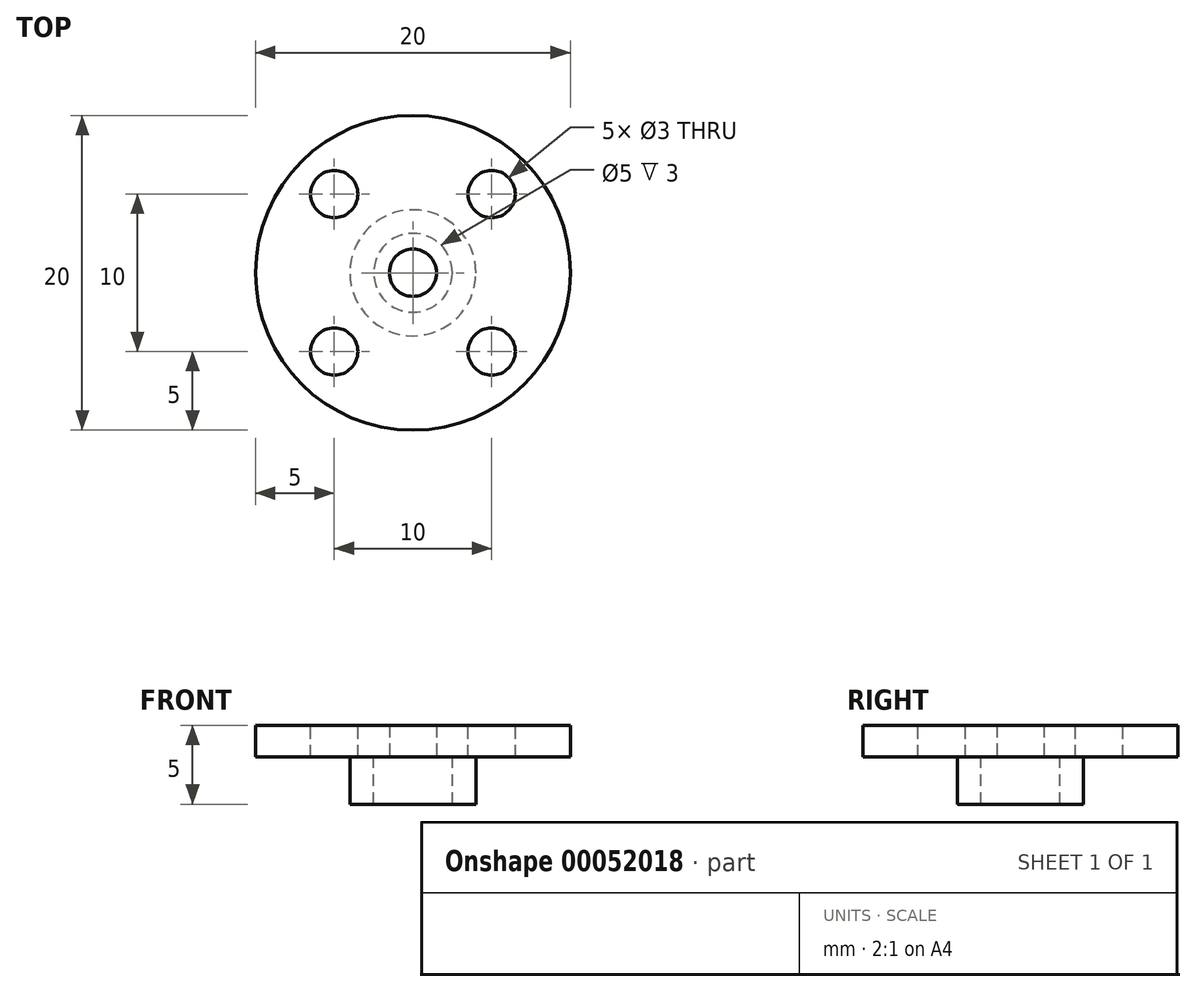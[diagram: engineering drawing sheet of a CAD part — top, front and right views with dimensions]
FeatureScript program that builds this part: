
annotation { "Feature Type Name" : "Feature", "Feature Type Description" : "" }
export const myFeature = defineFeature(function(context is Context, id is Id, definition is map)
    precondition{}
    {
        {
            var Q0;
            Q0=qCreatedBy(makeId("Top.planeOp"),FACE);
            var sketch = newSketch(context, id + "F0", { "sketchPlane" : qUnion([Q0])});
            skCircle(sketch, "E0", {"center": v(0, 0) * mm, "radius": 10 * mm});
            skCircle(sketch, "E1", {"center": v(0, 0) * mm, "radius": 1.5 * mm});
            skSolve(sketch);
        }
        {
            var Q0;
            Q0=makeQuery(id+"F0.imprint","IMPRINT",FACE,{"disambiguationData":[TD([[makeQuery(id+"F0.imprint","IMPRINT",EDGE,{"derivedFrom":sQuery(id+"F0.wireOp",EDGE,"E0")}),1.0]])]});
            extrude(context, id + "F1", {"entities" : qUnion([Q0]), "depth" : 2 * mm});
        }
        {
            var Q0;
            Q0=makeQuery(id+"F1.opExtrude","CAP_FACE",FACE,{"disambiguationData":[OSD([sQuery(id+"F0.wireOp",EDGE,"E0"),sQuery(id+"F0.wireOp",EDGE,"E1")])],"isStart":false});
            var sketch = newSketch(context, id + "F2", { "sketchPlane" : qUnion([Q0])});
            skLineSegment(sketch, "E2.bottom", {"start": v(-5, 5) * mm, "end": v(5, 5) * mm});
            skLineSegment(sketch, "E2.top", {"start": v(-5, -5) * mm, "end": v(5, -5) * mm});
            skLineSegment(sketch, "E2.left", {"start": v(-5, 5) * mm, "end": v(-5, -5) * mm});
            skLineSegment(sketch, "E2.right", {"start": v(5, 5) * mm, "end": v(5, -5) * mm});
            skLineSegment(sketch, "E3", {"start": v(-5, 5) * mm, "end": v(5, -5) * mm});
            skPoint(sketch, "E4", {"position": v(0, 0) * mm});
            skSolve(sketch);
        }
        {
            var Q0;
            Q0=sQuery(id+"F2.wireOp",VERTEX,"cc3338fc-096e-4a80-8973-da4a3b0933f0.1.0");
            var Q1;
            Q1=sQuery(id+"F2.wireOp",VERTEX,"793e61e9-3800-4246-b8c4-4b3496da24d5");
            var Q2;
            Q2=sQuery(id+"F2.wireOp",VERTEX,"cc3338fc-096e-4a80-8973-da4a3b0933f0.3.0");
            var Q3;
            Q3=sQuery(id+"F2.wireOp",VERTEX,"cc3338fc-096e-4a80-8973-da4a3b0933f0.2.0");
            var Q4;
            Q4=sQuery(id+"F2.wireOp",VERTEX,"E2.left.start");
            var Q5;
            Q5=sQuery(id+"F2.wireOp",VERTEX,"E2.right.start");
            var Q6;
            Q6=sQuery(id+"F2.wireOp",VERTEX,"E2.top.end");
            var Q7;
            Q7=sQuery(id+"F2.wireOp",VERTEX,"E2.left.end");
            var Q8;
            Q8=makeQuery(id+"F1.opExtrude","SWEPT_BODY",BODY,{"disambiguationData":[OSD([sQuery(id+"F0.wireOp",EDGE,"E0"),sQuery(id+"F0.wireOp",EDGE,"E1")])]});
            hole(context, id + "F3", {"style" : HoleStyle.SIMPLE, "holeDiameter" : 3 * mm, "endStyle" : HoleEndStyle.THROUGH, "locations" : qUnion([Q0, Q1, Q2, Q3, Q4, Q5, Q6, Q7]), "scope" : qUnion([Q8]), "isTappedThrough" : true});
        }
        {
            var Q0;
            Q0=makeQuery(id+"F1.opExtrude","CAP_FACE",FACE,{"disambiguationData":[OSD([sQuery(id+"F0.wireOp",EDGE,"E0"),sQuery(id+"F0.wireOp",EDGE,"E1")])],"isStart":true});
            var sketch = newSketch(context, id + "F4", { "sketchPlane" : qUnion([Q0])});
            skCircle(sketch, "E5", {"center": v(0, 0) * mm, "radius": 4 * mm});
            skCircle(sketch, "E6", {"center": v(0, 0) * mm, "radius": 2.5 * mm});
            skSolve(sketch);
        }
        {
            var Q0;
            Q0=makeQuery(id+"F4.imprint","IMPRINT",FACE,{"disambiguationData":[TD([[makeQuery(id+"F4.imprint","IMPRINT",EDGE,{"derivedFrom":sQuery(id+"F4.wireOp",EDGE,"E5")}),1.0]])]});
            extrude(context, id + "F5", {"entities" : qUnion([Q0]), "operationType" : NewBodyOperationType.ADD, "depth" : 3 * mm});
        }
    });
